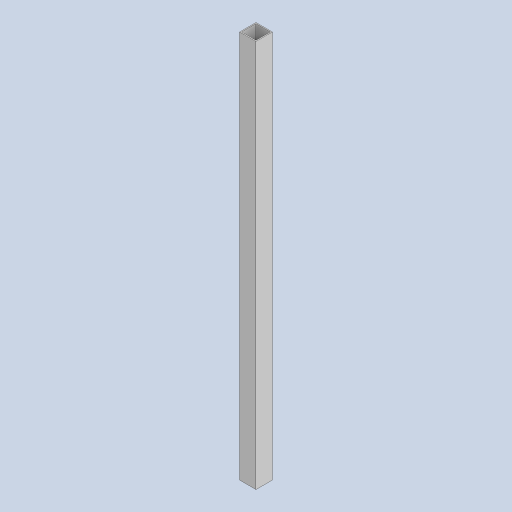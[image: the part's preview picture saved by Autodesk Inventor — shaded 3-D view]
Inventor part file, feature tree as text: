
AUTODESK INVENTOR PART (.ipt)
format: ipt  version: 2023 (Build 270158000, 158)  size: 84,992 bytes
history: native  units: mm
features: sketch x2, extrude x1
ambient origin geometry x8: Origin, YZ Plane, XZ Plane, XY Plane, X Axis, Y Axis, Z Axis, Center Point
bodies: Solid1 (feature_tree)
feature tree (3):
  sketch  "Sketch1"  dims[d0=25.4mm d1=25.4mm]
  extrude  "Extrusion1"  Depth=25.4mm
  sketch  "Sketch2"  dims[d2=1.5875mm d3=1.5875mm d4=600.0mm d5=0.0mm]
